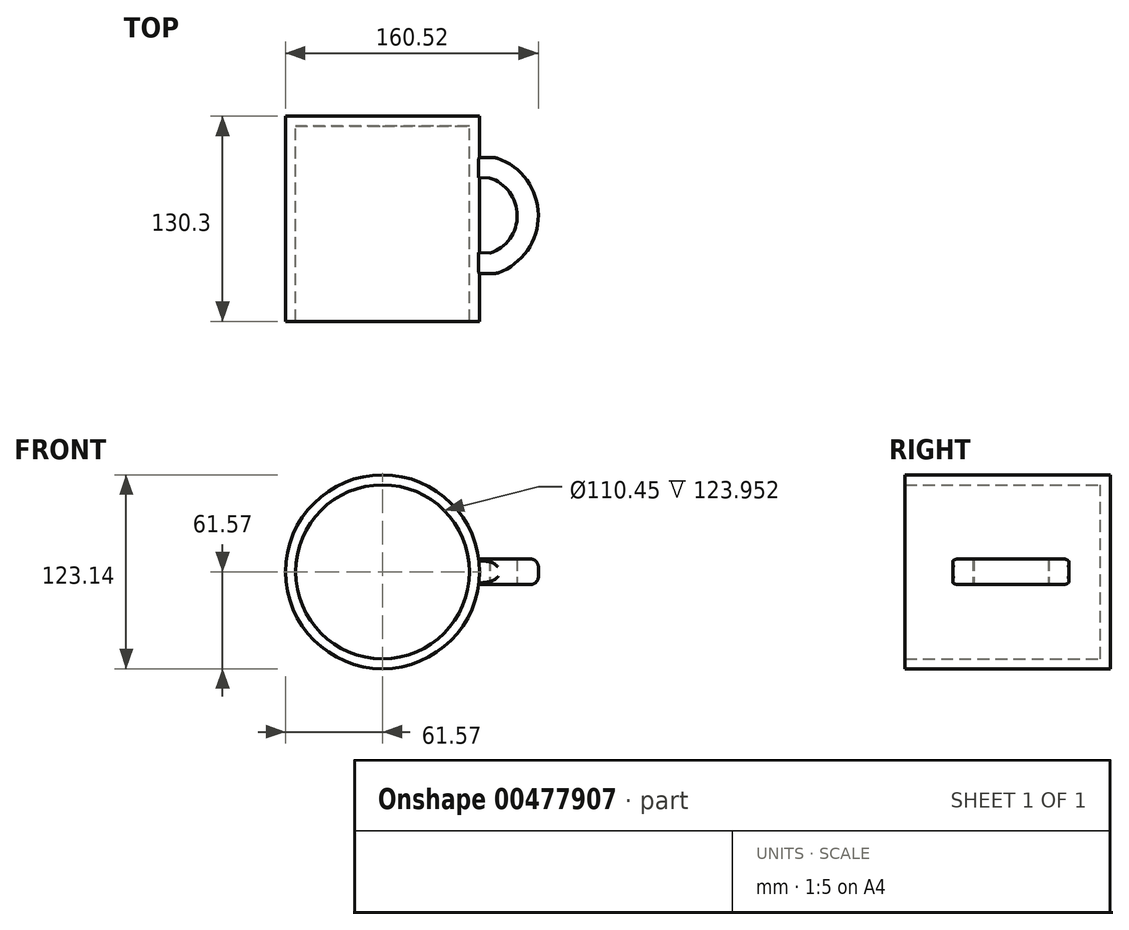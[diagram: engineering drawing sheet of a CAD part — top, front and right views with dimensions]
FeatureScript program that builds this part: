
annotation { "Feature Type Name" : "Feature", "Feature Type Description" : "" }
export const myFeature = defineFeature(function(context is Context, id is Id, definition is map)
    precondition{}
    {
        {
            var Q0;
            Q0=qCreatedBy(makeId("Front.planeOp"),FACE);
            var sketch = newSketch(context, id + "F0", { "sketchPlane" : qUnion([Q0])});
            skCircle(sketch, "E0", {"center": v(0, 0) * mm, "radius": 61.57 * mm});
            skSolve(sketch);
        }
        {
            var Q0;
            Q0 = qSketchRegion(id + "F0", true);
            extrude(context, id + "F1", {"entities" : qUnion([Q0]), "depth" : 130.3 * mm});
        }
        {
            var Q0;
            Q0=makeQuery(id+"F1.opExtrude","CAP_FACE",FACE,{"disambiguationData":[OSD([sQuery(id+"F0.wireOp",EDGE,"E0")])],"isStart":false});
            shell(context, id + "F2", {"entities" : qUnion([Q0]), "thickness" : 6.35 * mm});
        }
        {
            var Q0;
            Q0=qCreatedBy(makeId("Top.planeOp"),FACE);
            var sketch = newSketch(context, id + "F3", { "sketchPlane" : qUnion([Q0])});
            skArc(sketch, "E1.0", {"start": v(72.5, -99.78) * mm, "mid": v(98.95, -62.86) * mm, "end": v(71.88, -26.38) * mm});
            skArc(sketch, "E2.0", {"start": v(68.29, -87.06) * mm, "mid": v(85.55, -62.97) * mm, "end": v(67.89, -39.17) * mm});
            skLineSegment(sketch, "E3", {"start": v(72.5, -99.78) * mm, "end": v(59.09, -99.78) * mm});
            skLineSegment(sketch, "E4", {"start": v(59.09, -99.78) * mm, "end": v(59.09, -86.55) * mm});
            skLineSegment(sketch, "E5", {"start": v(59.09, -86.55) * mm, "end": v(68.29, -87.06) * mm});
            skLineSegment(sketch, "E6", {"start": v(71.88, -26.38) * mm, "end": v(59.06, -26.38) * mm});
            skLineSegment(sketch, "E7", {"start": v(59.06, -26.38) * mm, "end": v(59.06, -38.98) * mm});
            skLineSegment(sketch, "E8", {"start": v(59.06, -38.98) * mm, "end": v(67.89, -39.17) * mm});
            skSolve(sketch);
        }
        {
            var Q0;
            Q0 = qSketchRegion(id + "F3", true);
            extrude(context, id + "F4", {"entities" : qUnion([Q0]), "operationType" : NewBodyOperationType.ADD, "depth" : 16.26 * mm, "symmetric" : true});
        }
        {
            var Q0;
            Q0=makeQuery(id+"F4.opExtrude","SWEPT_FACE",FACE,{"disambiguationData":[OSD([sQuery(id+"F3.wireOp",EDGE,"E1.0")])]});
            fillet(context, id + "F5", {"entities" : qUnion([Q0]), "radius" : 5.08 * mm, "tangentPropagation" : true, "allowEdgeOverflow" : false});
        }
    });
